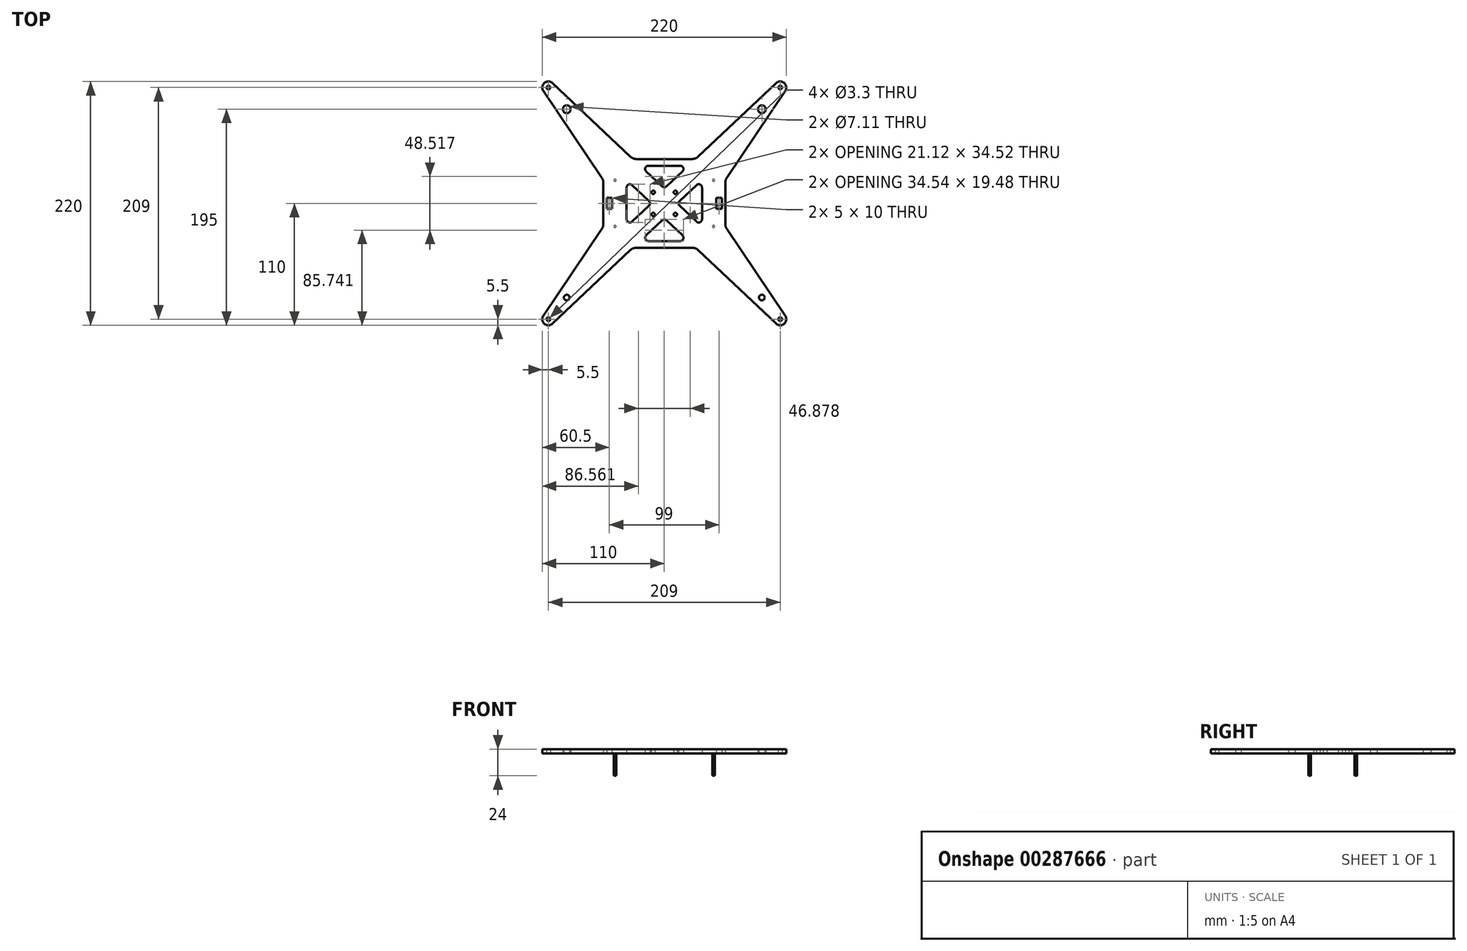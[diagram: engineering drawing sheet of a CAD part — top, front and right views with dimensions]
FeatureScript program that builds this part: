
annotation { "Feature Type Name" : "Feature", "Feature Type Description" : "" }
export const myFeature = defineFeature(function(context is Context, id is Id, definition is map)
    precondition{}
    {
        {
            var Q0;
            Q0=qCreatedBy(makeId("Top.planeOp"),FACE);
            var sketch = newSketch(context, id + "F0", { "sketchPlane" : qUnion([Q0])});
            skLineSegment(sketch, "E0", {"start": v(-28.94, 16.46) * mm, "end": v(-13.82, 2.18) * mm});
            skLineSegment(sketch, "E1", {"start": v(-13.82, -2.18) * mm, "end": v(-28.94, -16.46) * mm});
            skLineSegment(sketch, "E2", {"start": v(-34, -14.28) * mm, "end": v(-34, 14.28) * mm});
            skLineSegment(sketch, "E3", {"start": v(34, 14.28) * mm, "end": v(34, -14.28) * mm});
            skLineSegment(sketch, "E4", {"start": v(28.94, -16.46) * mm, "end": v(13.82, -2.18) * mm});
            skLineSegment(sketch, "E5", {"start": v(13.82, 2.18) * mm, "end": v(28.94, 16.46) * mm});
            skLineSegment(sketch, "E6", {"start": v(-16.34, -28.82) * mm, "end": v(-2.06, -15.34) * mm});
            skLineSegment(sketch, "E7", {"start": v(2.06, -15.34) * mm, "end": v(16.34, -28.82) * mm});
            skLineSegment(sketch, "E8", {"start": v(14.28, -34) * mm, "end": v(-14.28, -34) * mm});
            skLineSegment(sketch, "E9", {"start": v(16.34, 28.82) * mm, "end": v(2.06, 15.34) * mm});
            skLineSegment(sketch, "E10", {"start": v(-2.06, 15.34) * mm, "end": v(-16.34, 28.82) * mm});
            skLineSegment(sketch, "E11", {"start": v(-14.28, 34) * mm, "end": v(14.28, 34) * mm});
            skLineSegment(sketch, "E12", {"start": v(-47, -5) * mm, "end": v(-52, -5) * mm});
            skLineSegment(sketch, "E13", {"start": v(-52, -5) * mm, "end": v(-52, 5) * mm});
            skLineSegment(sketch, "E14", {"start": v(-52, 5) * mm, "end": v(-47, 5) * mm});
            skLineSegment(sketch, "E15", {"start": v(-47, 5) * mm, "end": v(-47, -5) * mm});
            skLineSegment(sketch, "E16", {"start": v(47, 5) * mm, "end": v(52, 5) * mm});
            skLineSegment(sketch, "E17", {"start": v(52, 5) * mm, "end": v(52, -5) * mm});
            skLineSegment(sketch, "E18", {"start": v(52, -5) * mm, "end": v(47, -5) * mm});
            skLineSegment(sketch, "E19", {"start": v(47, -5) * mm, "end": v(47, 5) * mm});
            skLineSegment(sketch, "E20", {"start": v(-55, 18.66) * mm, "end": v(-55, -18.66) * mm});
            skLineSegment(sketch, "E21", {"start": v(-56.36, -23.13) * mm, "end": v(-109.06, -101.43) * mm});
            skLineSegment(sketch, "E22", {"start": v(-100.72, -108.5) * mm, "end": v(-30.5, -42.18) * mm});
            skLineSegment(sketch, "E23", {"start": v(-25, -40) * mm, "end": v(25, -40) * mm});
            skLineSegment(sketch, "E24", {"start": v(30.5, -42.18) * mm, "end": v(100.72, -108.5) * mm});
            skLineSegment(sketch, "E25", {"start": v(109.06, -101.43) * mm, "end": v(56.36, -23.13) * mm});
            skLineSegment(sketch, "E26", {"start": v(55, -18.66) * mm, "end": v(55, 18.66) * mm});
            skLineSegment(sketch, "E27", {"start": v(56.36, 23.13) * mm, "end": v(109.06, 101.43) * mm});
            skLineSegment(sketch, "E28", {"start": v(100.72, 108.5) * mm, "end": v(30.5, 42.18) * mm});
            skLineSegment(sketch, "E29", {"start": v(25, 40) * mm, "end": v(-25, 40) * mm});
            skLineSegment(sketch, "E30", {"start": v(-30.5, 42.18) * mm, "end": v(-100.72, 108.5) * mm});
            skLineSegment(sketch, "E31", {"start": v(-109.06, 101.43) * mm, "end": v(-56.36, 23.13) * mm});
            skCircle(sketch, "E32", {"center": v(-87.97, 85) * mm, "radius": 3.56 * mm});
            skCircle(sketch, "E33", {"center": v(87.97, 85) * mm, "radius": 3.56 * mm});
            skCircle(sketch, "E34", {"center": v(-44.44, 20.81) * mm, "radius": 3.56 * mm});
            skCircle(sketch, "E35", {"center": v(44.44, 20.81) * mm, "radius": 3.56 * mm});
            skCircle(sketch, "E36", {"center": v(-87.97, -85) * mm, "radius": 2.55 * mm});
            skCircle(sketch, "E37", {"center": v(87.97, -85) * mm, "radius": 2.55 * mm});
            skCircle(sketch, "E38", {"center": v(-44.44, -20.8) * mm, "radius": 2.55 * mm});
            skCircle(sketch, "E39", {"center": v(44.44, -20.8) * mm, "radius": 2.55 * mm});
            skCircle(sketch, "E40", {"center": v(104.5, -104.5) * mm, "radius": 1.65 * mm});
            skCircle(sketch, "E41", {"center": v(-104.5, -104.5) * mm, "radius": 1.65 * mm});
            skCircle(sketch, "E42", {"center": v(104.5, 104.5) * mm, "radius": 1.65 * mm});
            skCircle(sketch, "E43", {"center": v(-104.5, 104.5) * mm, "radius": 1.65 * mm});
            skCircle(sketch, "E44", {"center": v(10, 10) * mm, "radius": 1.52 * mm});
            skCircle(sketch, "E45", {"center": v(10, -10) * mm, "radius": 1.52 * mm});
            skCircle(sketch, "E46", {"center": v(-10, -10) * mm, "radius": 1.52 * mm});
            skCircle(sketch, "E47", {"center": v(-10, 10) * mm, "radius": 1.52 * mm});
            skArc(sketch, "E48", {"start": v(-109.06, -101.43) * mm, "mid": v(-108.06, -108.7) * mm, "end": v(-100.72, -108.5) * mm});
            skArc(sketch, "E49", {"start": v(-100.72, 108.5) * mm, "mid": v(-108.06, 108.7) * mm, "end": v(-109.06, 101.43) * mm});
            skArc(sketch, "E50", {"start": v(109.06, 101.43) * mm, "mid": v(108.06, 108.7) * mm, "end": v(100.72, 108.5) * mm});
            skArc(sketch, "E51", {"start": v(100.72, -108.5) * mm, "mid": v(108.06, -108.7) * mm, "end": v(109.06, -101.43) * mm});
            skArc(sketch, "E52", {"start": v(-14.28, -34) * mm, "mid": v(-17.07, -32.1) * mm, "end": v(-16.34, -28.82) * mm});
            skArc(sketch, "E53", {"start": v(14.28, -34) * mm, "mid": v(17.07, -32.1) * mm, "end": v(16.34, -28.82) * mm});
            skArc(sketch, "E54", {"start": v(-2.06, -15.34) * mm, "mid": v(0, -14.52) * mm, "end": v(2.06, -15.34) * mm});
            skArc(sketch, "E55", {"start": v(13.82, 2.18) * mm, "mid": v(12.88, 0) * mm, "end": v(13.82, -2.18) * mm});
            skArc(sketch, "E56", {"start": v(28.94, -16.46) * mm, "mid": v(32.19, -17.03) * mm, "end": v(34, -14.28) * mm});
            skArc(sketch, "E57", {"start": v(28.94, 16.46) * mm, "mid": v(32.19, 17.03) * mm, "end": v(34, 14.28) * mm});
            skArc(sketch, "E58", {"start": v(-30.5, 42.18) * mm, "mid": v(-27.96, 40.57) * mm, "end": v(-25, 40) * mm});
            skArc(sketch, "E59", {"start": v(25, 40) * mm, "mid": v(27.96, 40.57) * mm, "end": v(30.5, 42.18) * mm});
            skArc(sketch, "E60", {"start": v(14.28, 34) * mm, "mid": v(17.07, 32.1) * mm, "end": v(16.34, 28.82) * mm});
            skArc(sketch, "E61", {"start": v(-14.28, 34) * mm, "mid": v(-17.07, 32.1) * mm, "end": v(-16.34, 28.82) * mm});
            skArc(sketch, "E62", {"start": v(-2.06, 15.34) * mm, "mid": v(0, 14.52) * mm, "end": v(2.06, 15.34) * mm});
            skArc(sketch, "E63", {"start": v(-56.36, 23.13) * mm, "mid": v(-55.35, 21) * mm, "end": v(-55, 18.66) * mm});
            skArc(sketch, "E64", {"start": v(-56.36, -23.13) * mm, "mid": v(-55.35, -21) * mm, "end": v(-55, -18.66) * mm});
            skArc(sketch, "E65", {"start": v(-34, 14.28) * mm, "mid": v(-32.19, 17.03) * mm, "end": v(-28.94, 16.46) * mm});
            skArc(sketch, "E66", {"start": v(-34, -14.28) * mm, "mid": v(-32.19, -17.03) * mm, "end": v(-28.94, -16.46) * mm});
            skArc(sketch, "E67", {"start": v(-13.82, 2.18) * mm, "mid": v(-12.88, 0) * mm, "end": v(-13.82, -2.18) * mm});
            skArc(sketch, "E68", {"start": v(-30.5, -42.18) * mm, "mid": v(-27.96, -40.57) * mm, "end": v(-25, -40) * mm});
            skArc(sketch, "E69", {"start": v(25, -40) * mm, "mid": v(27.96, -40.57) * mm, "end": v(30.5, -42.18) * mm});
            skArc(sketch, "E70", {"start": v(55, -18.66) * mm, "mid": v(55.35, -21) * mm, "end": v(56.36, -23.13) * mm});
            skArc(sketch, "E71", {"start": v(55, 18.66) * mm, "mid": v(55.35, 21) * mm, "end": v(56.36, 23.13) * mm});
            skSolve(sketch);
        }
        {
            var Q0;
            Q0=makeQuery(id+"F0.imprint","IMPRINT",FACE,{"disambiguationData":[TD([[makeQuery(id+"F0.imprint","IMPRINT",EDGE,{"derivedFrom":sQuery(id+"F0.wireOp",EDGE,"E0")}),1.0]])]});
            extrude(context, id + "F1", {"entities" : qUnion([Q0]), "depth" : 4 * mm, "offsetDistance" : 25 * mm});
        }
        {
            var Q0;
            Q0=qCreatedBy(makeId("Top.planeOp"),FACE);
            var sketch = newSketch(context, id + "F2", { "sketchPlane" : qUnion([Q0])});
            skCircle(sketch, "E72", {"center": v(-44.44, 20.81) * mm, "radius": 1 * mm});
            skCircle(sketch, "E73", {"center": v(-44.44, -20.8) * mm, "radius": 1 * mm});
            skCircle(sketch, "E74", {"center": v(44.44, 20.81) * mm, "radius": 1 * mm});
            skCircle(sketch, "E75", {"center": v(44.44, -20.8) * mm, "radius": 1 * mm});
            skSolve(sketch);
        }
        {
            var Q0;
            Q0 = qSketchRegion(id + "F2", true);
            extrude(context, id + "F3", {"entities" : qUnion([Q0]), "oppositeDirection" : true, "depth" : 20 * mm, "offsetDistance" : 25 * mm});
        }
        {
            var Q0;
            Q0=makeQuery(id+"F1.opExtrude","CAP_FACE",FACE,{"disambiguationData":[OSD([sQuery(id+"F0.wireOp",EDGE,"E0"),sQuery(id+"F0.wireOp",EDGE,"E1"),sQuery(id+"F0.wireOp",EDGE,"E2"),sQuery(id+"F0.wireOp",EDGE,"E3"),sQuery(id+"F0.wireOp",EDGE,"E4"),sQuery(id+"F0.wireOp",EDGE,"E5"),sQuery(id+"F0.wireOp",EDGE,"E6"),sQuery(id+"F0.wireOp",EDGE,"E7"),sQuery(id+"F0.wireOp",EDGE,"E8"),sQuery(id+"F0.wireOp",EDGE,"E9"),sQuery(id+"F0.wireOp",EDGE,"E10"),sQuery(id+"F0.wireOp",EDGE,"E11"),sQuery(id+"F0.wireOp",EDGE,"E12"),sQuery(id+"F0.wireOp",EDGE,"E13"),sQuery(id+"F0.wireOp",EDGE,"E14"),sQuery(id+"F0.wireOp",EDGE,"E15"),sQuery(id+"F0.wireOp",EDGE,"E16"),sQuery(id+"F0.wireOp",EDGE,"E17"),sQuery(id+"F0.wireOp",EDGE,"E18"),sQuery(id+"F0.wireOp",EDGE,"E19"),sQuery(id+"F0.wireOp",EDGE,"E20"),sQuery(id+"F0.wireOp",EDGE,"E21"),sQuery(id+"F0.wireOp",EDGE,"E22"),sQuery(id+"F0.wireOp",EDGE,"E23"),sQuery(id+"F0.wireOp",EDGE,"E24"),sQuery(id+"F0.wireOp",EDGE,"E25"),sQuery(id+"F0.wireOp",EDGE,"E26"),sQuery(id+"F0.wireOp",EDGE,"E27"),sQuery(id+"F0.wireOp",EDGE,"E28"),sQuery(id+"F0.wireOp",EDGE,"E29"),sQuery(id+"F0.wireOp",EDGE,"E30"),sQuery(id+"F0.wireOp",EDGE,"E31"),sQuery(id+"F0.wireOp",EDGE,"E32"),sQuery(id+"F0.wireOp",EDGE,"E33"),sQuery(id+"F0.wireOp",EDGE,"E34"),sQuery(id+"F0.wireOp",EDGE,"E35"),sQuery(id+"F0.wireOp",EDGE,"E36"),sQuery(id+"F0.wireOp",EDGE,"E37"),sQuery(id+"F0.wireOp",EDGE,"E38"),sQuery(id+"F0.wireOp",EDGE,"E39"),sQuery(id+"F0.wireOp",EDGE,"E40"),sQuery(id+"F0.wireOp",EDGE,"E41"),sQuery(id+"F0.wireOp",EDGE,"E42"),sQuery(id+"F0.wireOp",EDGE,"E43"),sQuery(id+"F0.wireOp",EDGE,"E44"),sQuery(id+"F0.wireOp",EDGE,"E45"),sQuery(id+"F0.wireOp",EDGE,"E46"),sQuery(id+"F0.wireOp",EDGE,"E47"),sQuery(id+"F0.wireOp",EDGE,"E48"),sQuery(id+"F0.wireOp",EDGE,"E49"),sQuery(id+"F0.wireOp",EDGE,"E50"),sQuery(id+"F0.wireOp",EDGE,"E51"),sQuery(id+"F0.wireOp",EDGE,"E52"),sQuery(id+"F0.wireOp",EDGE,"E53"),sQuery(id+"F0.wireOp",EDGE,"E54"),sQuery(id+"F0.wireOp",EDGE,"E55"),sQuery(id+"F0.wireOp",EDGE,"E56"),sQuery(id+"F0.wireOp",EDGE,"E57"),sQuery(id+"F0.wireOp",EDGE,"E58"),sQuery(id+"F0.wireOp",EDGE,"E59"),sQuery(id+"F0.wireOp",EDGE,"E60"),sQuery(id+"F0.wireOp",EDGE,"E61"),sQuery(id+"F0.wireOp",EDGE,"E62"),sQuery(id+"F0.wireOp",EDGE,"E63"),sQuery(id+"F0.wireOp",EDGE,"E64"),sQuery(id+"F0.wireOp",EDGE,"E65"),sQuery(id+"F0.wireOp",EDGE,"E66"),sQuery(id+"F0.wireOp",EDGE,"E67"),sQuery(id+"F0.wireOp",EDGE,"E68"),sQuery(id+"F0.wireOp",EDGE,"E69"),sQuery(id+"F0.wireOp",EDGE,"E70"),sQuery(id+"F0.wireOp",EDGE,"E71")])],"isStart":false});
            var sketch = newSketch(context, id + "F4", { "sketchPlane" : qUnion([Q0])});
            skCircle(sketch, "E76.0", {"center": v(44.44, 20.81) * mm, "radius": 3.56 * mm});
            skCircle(sketch, "E77.0", {"center": v(44.44, -20.8) * mm, "radius": 2.55 * mm});
            skCircle(sketch, "E78.0", {"center": v(-44.44, -20.8) * mm, "radius": 2.55 * mm});
            skCircle(sketch, "E79.0", {"center": v(-44.44, 20.81) * mm, "radius": 3.56 * mm});
            skSolve(sketch);
        }
        {
            var Q0;
            Q0 = qSketchRegion(id + "F4", true);
            extrude(context, id + "F5", {"entities" : qUnion([Q0]), "operationType" : NewBodyOperationType.ADD, "oppositeDirection" : true, "depth" : 4 * mm, "offsetDistance" : 25 * mm});
        }
    });
